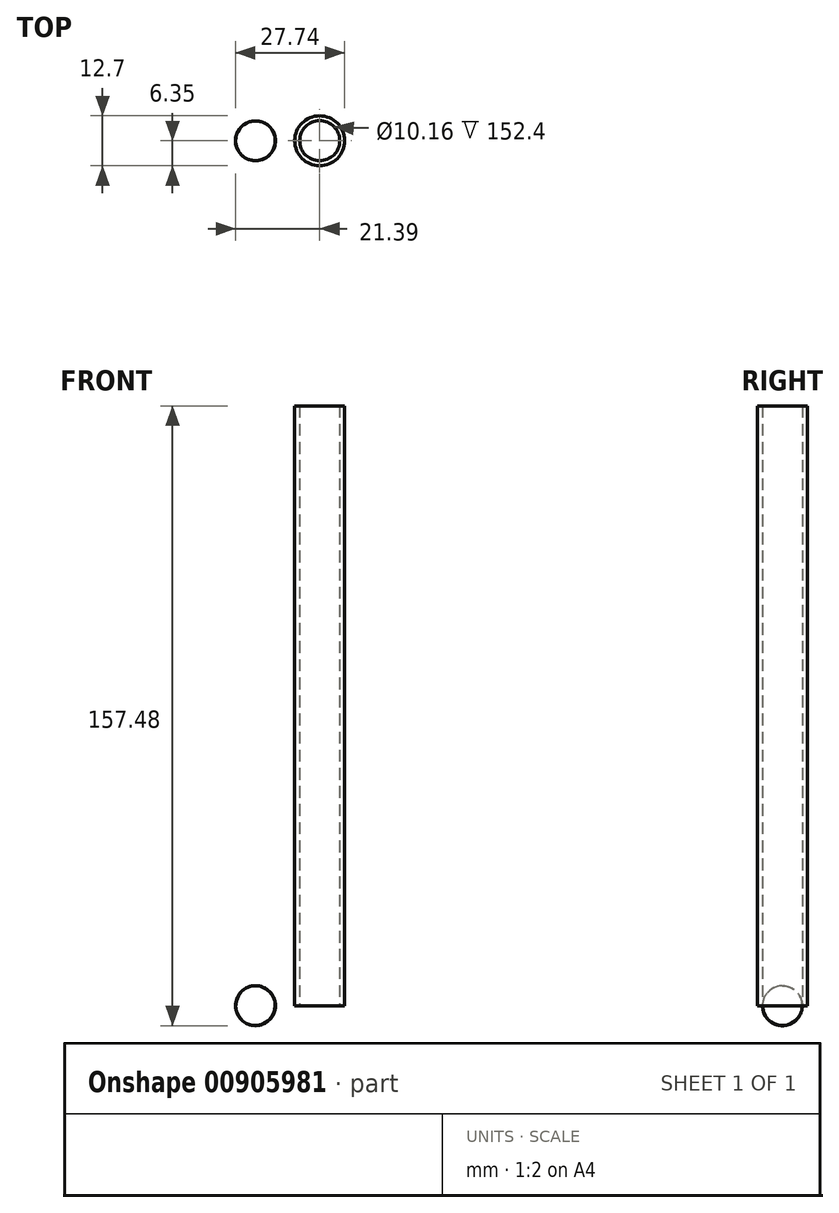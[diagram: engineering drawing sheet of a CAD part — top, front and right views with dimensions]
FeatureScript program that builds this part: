
annotation { "Feature Type Name" : "Feature", "Feature Type Description" : "" }
export const myFeature = defineFeature(function(context is Context, id is Id, definition is map)
    precondition{}
    {
        {
            var Q0;
            Q0=qCreatedBy(makeId("Top.planeOp"),FACE);
            var sketch = newSketch(context, id + "F0", { "sketchPlane" : qUnion([Q0])});
            skCircle(sketch, "E0", {"center": v(0, 0) * mm, "radius": 6.35 * mm});
            skCircle(sketch, "E1", {"center": v(0, 0) * mm, "radius": 5.08 * mm});
            skArc(sketch, "E2", {"start": v(-16.31, -5.05) * mm, "mid": v(-11.29, 0) * mm, "end": v(-16.31, 5.05) * mm});
            skLineSegment(sketch, "E3", {"start": v(-16.31, -5.05) * mm, "end": v(-16.31, 5.05) * mm});
            skSolve(sketch);
        }
        {
            var Q0;
            Q0=makeQuery(id+"F0.imprint","IMPRINT",FACE,{"disambiguationData":[TD([[makeQuery(id+"F0.imprint","IMPRINT",EDGE,{"derivedFrom":sQuery(id+"F0.wireOp",EDGE,"E0")}),1.0]])]});
            extrude(context, id + "F1", {"entities" : qUnion([Q0]), "depth" : 152.4 * mm, "offsetDistance" : 25.4 * mm});
        }
        {
            var Q0;
            Q0=makeQuery(id+"F0.imprint","IMPRINT",FACE,{"disambiguationData":[TD([[makeQuery(id+"F0.imprint","IMPRINT",EDGE,{"derivedFrom":sQuery(id+"F0.wireOp",EDGE,"E2")}),1.0]])]});
            var Q1;
            Q1=sQuery(id+"F0.wireOp",EDGE,"E3");
            revolve(context, id + "F2", {"surfaceOperationType" : NewSurfaceOperationType.NEW, "entities" : qUnion([Q0]), "axis" : qUnion([Q1]), "revolveType" : RevolveType.ONE_DIRECTION, "angle" : 360 * degree});
        }
    });
